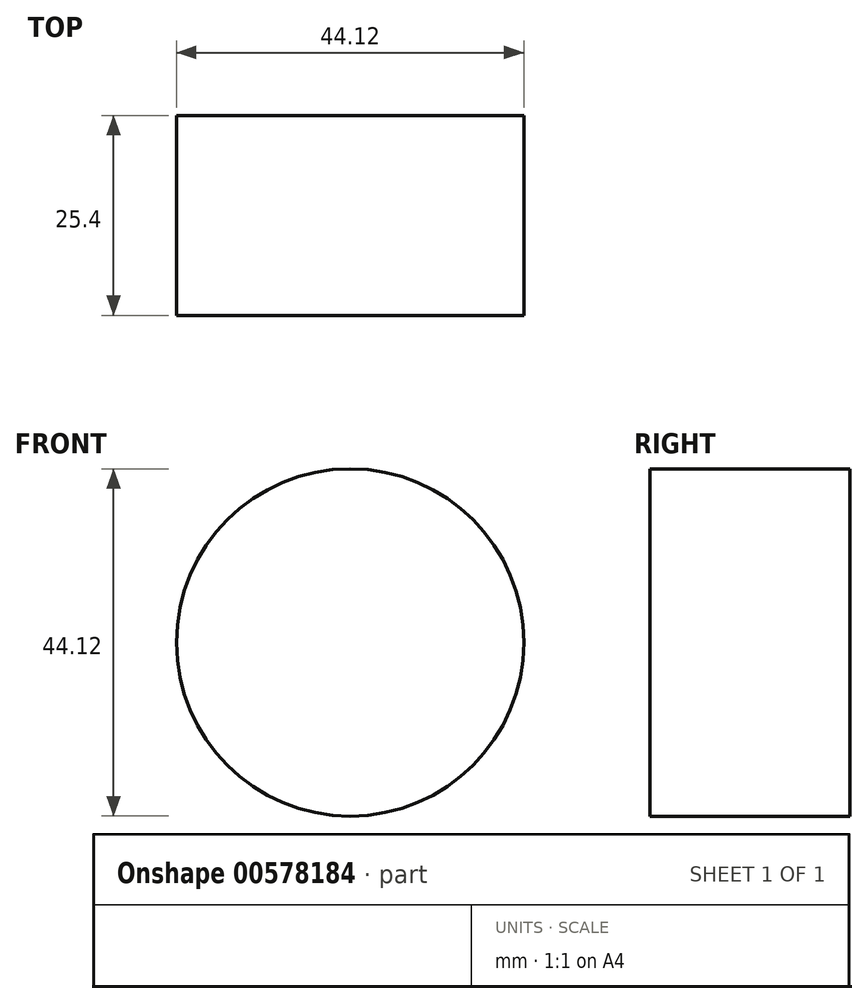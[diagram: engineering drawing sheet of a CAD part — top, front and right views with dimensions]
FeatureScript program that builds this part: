
annotation { "Feature Type Name" : "Feature", "Feature Type Description" : "" }
export const myFeature = defineFeature(function(context is Context, id is Id, definition is map)
    precondition{}
    {
        {
            var Q0;
            Q0=qCreatedBy(makeId("Front.planeOp"),FACE);
            var sketch = newSketch(context, id + "F0", { "sketchPlane" : qUnion([Q0])});
            skCircle(sketch, "E0", {"center": v(0, 0) * mm, "radius": 22.06 * mm});
            skSolve(sketch);
        }
        {
            var Q0;
            Q0 = qSketchRegion(id + "F0", true);
            extrude(context, id + "F1", {"entities" : qUnion([Q0]), "depth" : 25.4 * mm, "offsetDistance" : 25.4 * mm});
        }
    });
